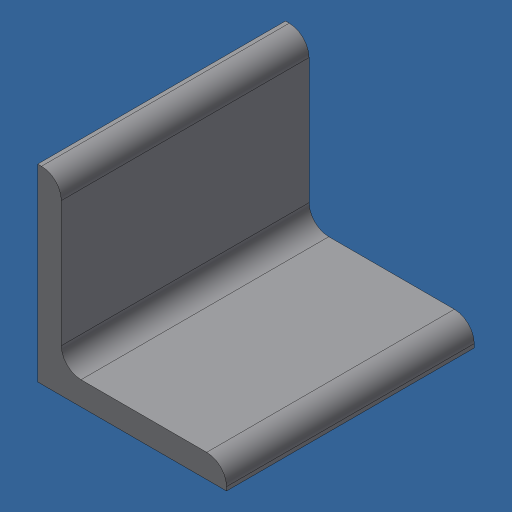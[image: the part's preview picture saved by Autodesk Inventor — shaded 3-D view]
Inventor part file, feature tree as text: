
AUTODESK INVENTOR PART (.ipt)
format: ipt  version: 2024.3 (Build 283343000, 343)  size: 124,416 bytes
history: native  units: mm (DEFAULTED — no unit token found)
features: other x1, extrude x1
ambient origin geometry x8: Origin, YZ Plane, XZ Plane, XY Plane, X Axis, Y Axis, Z Axis, Center Point
bodies: Body1 (feature_tree)
feature tree (2):
  other  "Finish - None"
  extrude  "3" X 3" X 3/8""  Depth=9.525mm
